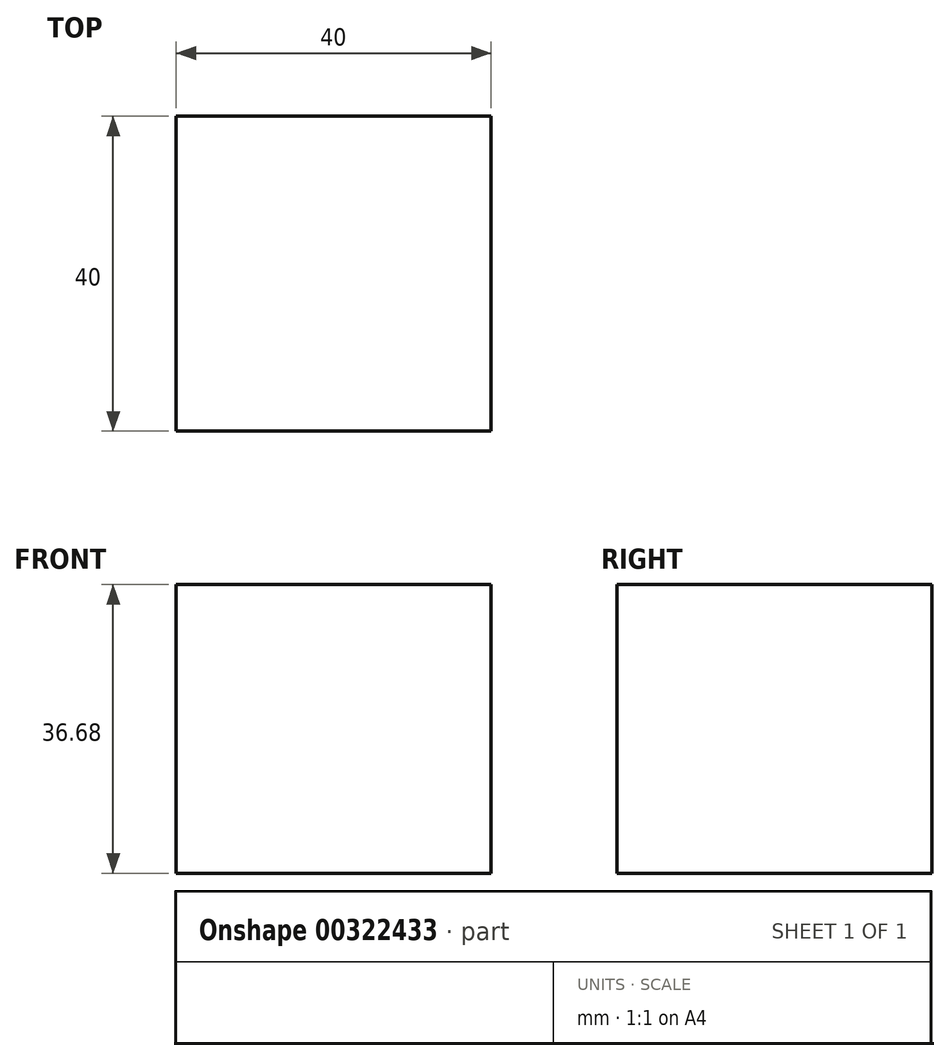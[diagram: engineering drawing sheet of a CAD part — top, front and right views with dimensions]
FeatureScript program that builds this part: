
annotation { "Feature Type Name" : "Feature", "Feature Type Description" : "" }
export const myFeature = defineFeature(function(context is Context, id is Id, definition is map)
    precondition{}
    {
        {
            var Q0;
            Q0=qCreatedBy(makeId("Right.planeOp"),FACE);
            var sketch = newSketch(context, id + "F0", { "sketchPlane" : qUnion([Q0])});
            skLineSegment(sketch, "E0.bottom", {"start": v(0, 0) * mm, "end": v(-40, 0) * mm});
            skLineSegment(sketch, "E0.top", {"start": v(0, 36.68) * mm, "end": v(-40, 36.68) * mm});
            skLineSegment(sketch, "E0.left", {"start": v(0, 0) * mm, "end": v(0, 36.68) * mm});
            skLineSegment(sketch, "E0.right", {"start": v(-40, 0) * mm, "end": v(-40, 36.68) * mm});
            skSolve(sketch);
        }
        {
            var Q0;
            Q0=makeQuery(id+"F0.imprint","IMPRINT",FACE,{"disambiguationData":[TD([[makeQuery(id+"F0.imprint","IMPRINT",EDGE,{"derivedFrom":sQuery(id+"F0.wireOp",EDGE,"E0.bottom")}),-1.0]])]});
            extrude(context, id + "F1", {"entities" : qUnion([Q0]), "depth" : 40 * mm});
        }
    });
